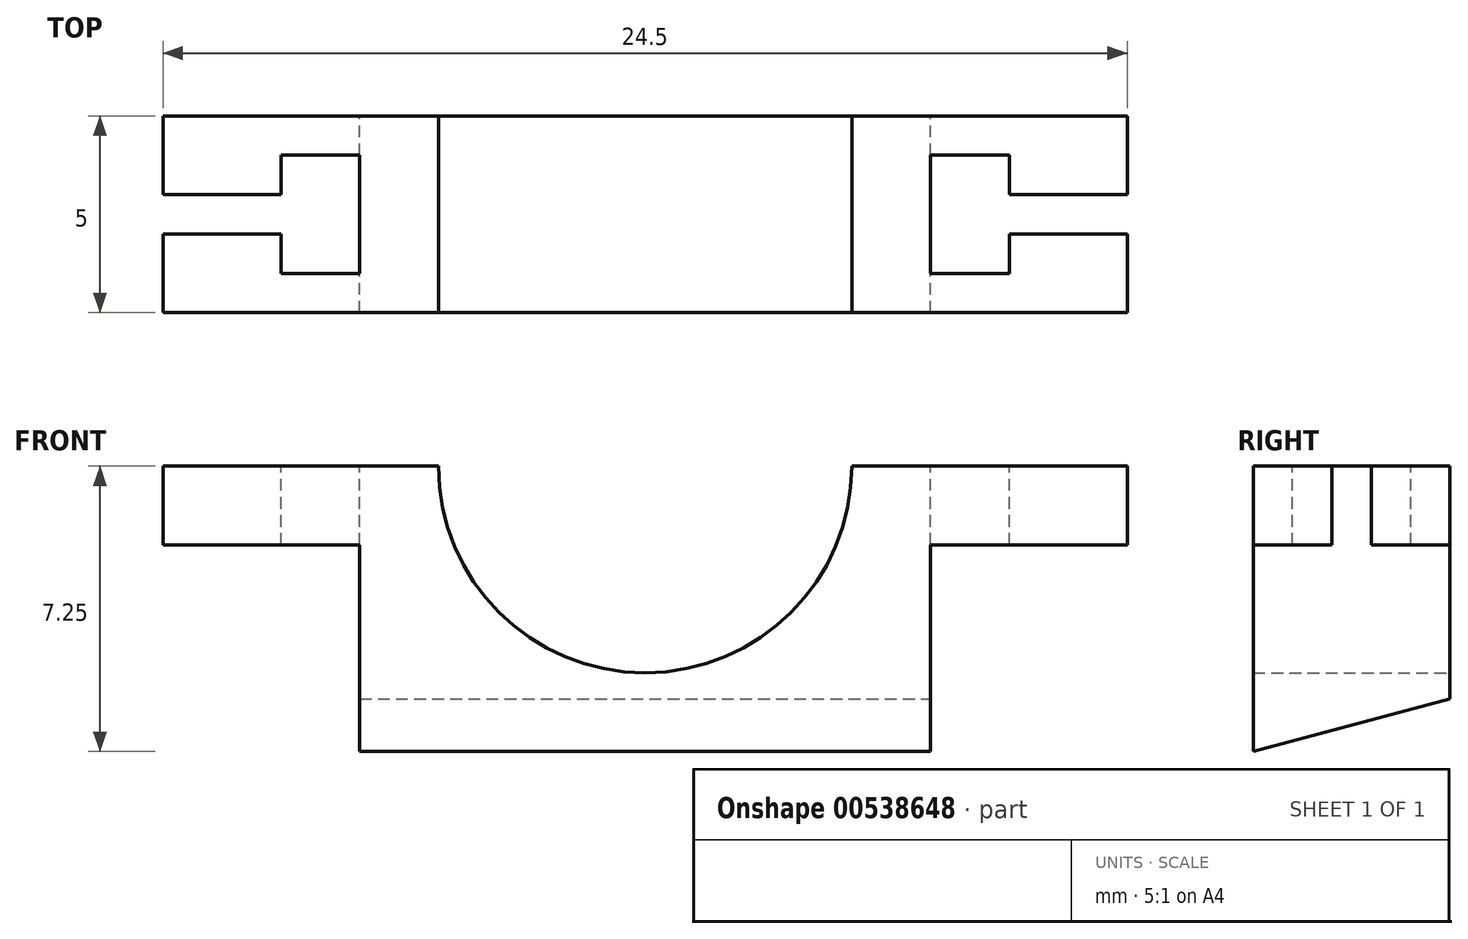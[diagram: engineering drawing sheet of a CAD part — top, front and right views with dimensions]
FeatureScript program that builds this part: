
annotation { "Feature Type Name" : "Feature", "Feature Type Description" : "" }
export const myFeature = defineFeature(function(context is Context, id is Id, definition is map)
    precondition{}
    {
        {
            var Q0;
            Q0=qCreatedBy(makeId("Front.planeOp"),FACE);
            var sketch = newSketch(context, id + "F0", { "sketchPlane" : qUnion([Q0])});
            skArc(sketch, "E0", {"start": v(-5.25, 0) * mm, "mid": v(0, -5.25) * mm, "end": v(5.25, 0) * mm});
            skArc(sketch, "E1", {"start": v(-7.25, 0) * mm, "mid": v(0, -7.25) * mm, "end": v(7.25, 0) * mm});
            skLineSegment(sketch, "E2", {"start": v(-7.25, 0) * mm, "end": v(-5.25, 0) * mm});
            skLineSegment(sketch, "E3", {"start": v(5.25, 0) * mm, "end": v(7.25, 0) * mm});
            skLineSegment(sketch, "E4.top", {"start": v(-7.25, -7.25) * mm, "end": v(7.25, -7.25) * mm});
            skLineSegment(sketch, "E4.left", {"start": v(-7.25, 0) * mm, "end": v(-7.25, -7.25) * mm});
            skLineSegment(sketch, "E4.right", {"start": v(7.25, 0) * mm, "end": v(7.25, -7.25) * mm});
            skLineSegment(sketch, "E5", {"start": v(7.25, 0) * mm, "end": v(12.25, 0) * mm});
            skLineSegment(sketch, "E6", {"start": v(12.25, 0) * mm, "end": v(12.25, -2) * mm});
            skLineSegment(sketch, "E7", {"start": v(12.25, -2) * mm, "end": v(7.25, -2) * mm});
            skLineSegment(sketch, "E8", {"start": v(-7.25, 0) * mm, "end": v(-12.25, 0) * mm});
            skLineSegment(sketch, "E9", {"start": v(-12.25, 0) * mm, "end": v(-12.25, -2) * mm});
            skLineSegment(sketch, "E10", {"start": v(-12.25, -2) * mm, "end": v(-7.25, -2) * mm});
            skSolve(sketch);
        }
        {
            var Q0;
            Q0=qSketchRegion(id+"F0",true);
            extrude(context, id + "F1", {"entities" : qUnion([Q0]), "endBound" : BoundingType.SYMMETRIC, "depth" : 5 * mm, "offsetDistance" : 25 * mm});
        }
        {
            var Q0;
            Q0=qCreatedBy(makeId("Top.planeOp"),FACE);
            var sketch = newSketch(context, id + "F2", { "sketchPlane" : qUnion([Q0])});
            skLineSegment(sketch, "E11.bottom", {"start": v(-12.25, 0.5) * mm, "end": v(-7.25, 0.5) * mm});
            skLineSegment(sketch, "E11.top", {"start": v(-12.25, -0.5) * mm, "end": v(-7.25, -0.5) * mm});
            skLineSegment(sketch, "E11.left", {"start": v(-12.25, 0.5) * mm, "end": v(-12.25, -0.5) * mm});
            skLineSegment(sketch, "E11.right", {"start": v(-7.25, 0.5) * mm, "end": v(-7.25, -0.5) * mm});
            skPoint(sketch, "E12", {"position": v(-12.25, 0) * mm});
            skLineSegment(sketch, "E13.bottom", {"start": v(-9.25, 1.5) * mm, "end": v(-7.25, 1.5) * mm});
            skLineSegment(sketch, "E13.top", {"start": v(-9.25, -1.5) * mm, "end": v(-7.25, -1.5) * mm});
            skLineSegment(sketch, "E13.left", {"start": v(-9.25, 1.5) * mm, "end": v(-9.25, -1.5) * mm});
            skLineSegment(sketch, "E13.right", {"start": v(-7.25, 1.5) * mm, "end": v(-7.25, -1.5) * mm});
            skPoint(sketch, "E13.middle", {"position": v(-8.25, 0) * mm});
            skLineSegment(sketch, "E14.MirrorCS", {"start": v(12.25, 0.5) * mm, "end": v(12.25, -0.5) * mm});
            skPoint(sketch, "E15.MirrorP", {"position": v(12.25, 0) * mm});
            skLineSegment(sketch, "E16.MirrorCS", {"start": v(7.25, 1.5) * mm, "end": v(7.25, -1.5) * mm});
            skLineSegment(sketch, "E17.MirrorCS", {"start": v(9.25, 1.5) * mm, "end": v(9.25, -1.5) * mm});
            skLineSegment(sketch, "E18.MirrorCS", {"start": v(9.25, -1.5) * mm, "end": v(7.25, -1.5) * mm});
            skPoint(sketch, "E19.MirrorP", {"position": v(8.25, 0) * mm});
            skLineSegment(sketch, "E20.MirrorCS", {"start": v(9.25, 1.5) * mm, "end": v(7.25, 1.5) * mm});
            skLineSegment(sketch, "E21.MirrorCS", {"start": v(7.25, 0.5) * mm, "end": v(7.25, -0.5) * mm});
            skLineSegment(sketch, "E22.MirrorCS", {"start": v(12.25, -0.5) * mm, "end": v(7.25, -0.5) * mm});
            skLineSegment(sketch, "E23.MirrorCS", {"start": v(12.25, 0.5) * mm, "end": v(7.25, 0.5) * mm});
            skSolve(sketch);
        }
        {
            var Q0;
            Q0=qSketchRegion(id+"F2",true);
            extrude(context, id + "F3", {"entities" : qUnion([Q0]), "operationType" : NewBodyOperationType.REMOVE, "oppositeDirection" : true, "depth" : 25 * mm, "offsetDistance" : 25 * mm});
        }
        {
            var Q0;
            Q0=makeQuery(id+"F3.boolean.opBoolean","MERGE",FACE,{"derivedFrom":[makeQuery(id+"F1.opExtrude","SWEPT_FACE",FACE,{"disambiguationData":[OSD([sQuery(id+"F0.wireOp",EDGE,"E4.right")])]}),makeQuery(id+"F3.opExtrude","SWEPT_FACE",FACE,{"disambiguationData":[OSD([sQuery(id+"F2.wireOp",EDGE,"E16.MirrorCS"),sQuery(id+"F2.wireOp",EDGE,"E21.MirrorCS")])]})]});
            var sketch = newSketch(context, id + "F4", { "sketchPlane" : qUnion([Q0])});
            skLineSegment(sketch, "E24", {"start": v(5.18, -7.25) * mm, "end": v(-2.5, -7.25) * mm, "construction": true});
            skLineSegment(sketch, "E25", {"start": v(-2.5, -7.25) * mm, "end": v(12.55, -3.22) * mm, "construction": true});
            skLineSegment(sketch, "E26", {"start": v(2.5, -5.91) * mm, "end": v(2.5, -7.25) * mm});
            skLineSegment(sketch, "E27", {"start": v(2.5, -5.91) * mm, "end": v(-2.5, -7.25) * mm});
            skLineSegment(sketch, "E28", {"start": v(-2.5, -7.25) * mm, "end": v(2.5, -7.25) * mm});
            skSolve(sketch);
        }
        {
            var Q0;
            Q0=qSketchRegion(id+"F4",true);
            extrude(context, id + "F5", {"entities" : qUnion([Q0]), "operationType" : NewBodyOperationType.REMOVE, "oppositeDirection" : true, "depth" : 25 * mm, "offsetDistance" : 25 * mm});
        }
    });
